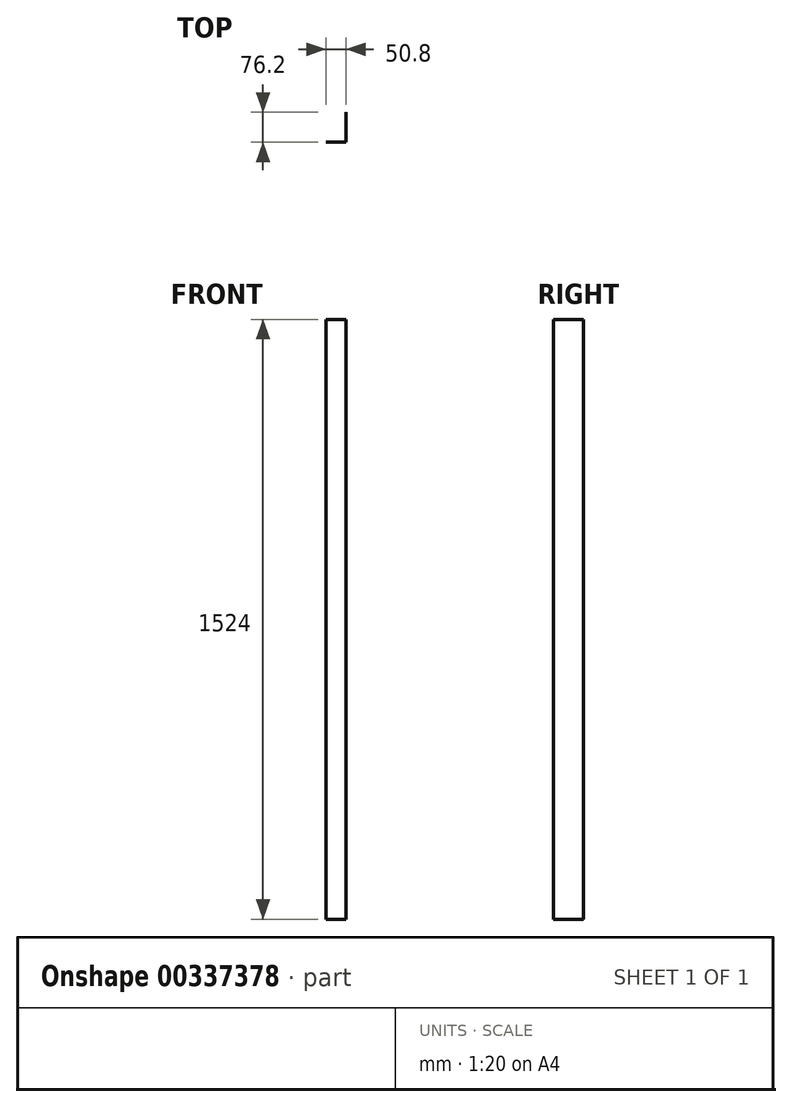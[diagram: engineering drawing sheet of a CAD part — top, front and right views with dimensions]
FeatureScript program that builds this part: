
annotation { "Feature Type Name" : "Feature", "Feature Type Description" : "" }
export const myFeature = defineFeature(function(context is Context, id is Id, definition is map)
    precondition{}
    {
        {
            var Q0;
            Q0=qCreatedBy(makeId("Top.planeOp"),FACE);
            var sketch = newSketch(context, id + "F0", { "sketchPlane" : qUnion([Q0])});
            skLineSegment(sketch, "E0", {"start": v(-68.4, -52.54) * mm, "end": v(-17.6, -52.54) * mm});
            skLineSegment(sketch, "E1", {"start": v(-17.6, -52.54) * mm, "end": v(-17.6, 23.66) * mm});
            skSolve(sketch);
        }
        {
            var Q0;
            Q0 = qSketchRegion(id + "F0", true);
            var Q1;
            Q1=sQuery(id+"F0.wireOp",EDGE,"E1");
            var Q2;
            Q2=sQuery(id+"F0.wireOp",EDGE,"E0");
            extrude(context, id + "F1", {"entities" : qUnion([Q0]), "bodyType" : ToolBodyType.SURFACE, "surfaceEntities" : qUnion([Q1, Q2]), "depth" : 1524 * mm});
        }
    });
